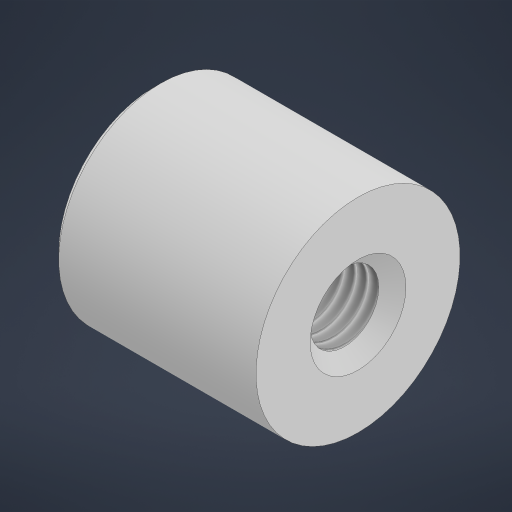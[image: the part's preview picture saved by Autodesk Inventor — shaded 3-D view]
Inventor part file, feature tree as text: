
AUTODESK INVENTOR PART (.ipt)
format: ipt  version: 2024.1 (Build 281209000, 209)  size: 188,928 bytes
history: native  units: mm
features: sketch x2, revolve x1, hole x1, chamfer x1
ambient origin geometry x8: Origin, YZ Plane, XZ Plane, XY Plane, X Axis, Y Axis, Z Axis, Center Point
bodies: Solid1 (feature_tree)
feature tree (5):
  revolve  "Revolution1"  [1 undecoded]
  hole  "Hole1"  [1 undecoded]
  chamfer  "Chamfer1"  [1 undecoded]
  sketch  "Sketch1"  dims[d0=30.0mm d1=30.0mm]
  sketch  "Sketch2"  dims[d2=90.0deg d3=10.106mm d4=10.0mm d5=14.1mm d6=2.0mm d7=90.0deg d8=15.0mm d9=20.594885mm d10=1.0mm d11=2.0mm d12=45.0deg]
note: 3 required parameter values undecoded (feature->parameter linkage not recoverable at this tier; creation-order binding heuristic only, values carry confidence <= 0.55)